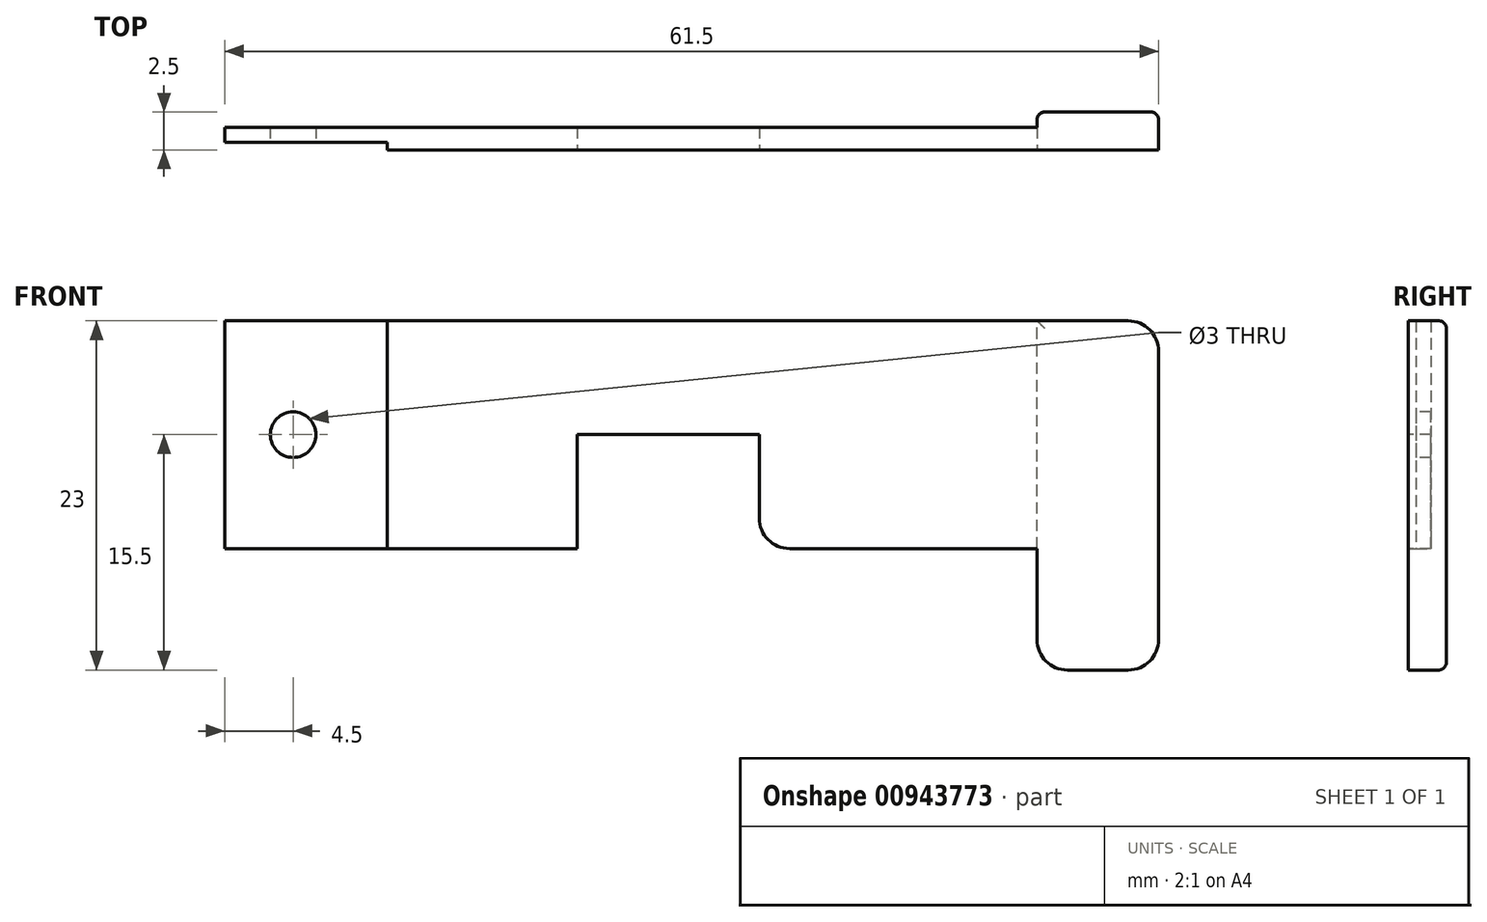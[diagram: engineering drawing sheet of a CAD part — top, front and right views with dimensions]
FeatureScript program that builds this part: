
annotation { "Feature Type Name" : "Feature", "Feature Type Description" : "" }
export const myFeature = defineFeature(function(context is Context, id is Id, definition is map)
    precondition{}
    {
        {
            var Q0;
            Q0=qCreatedBy(makeId("Front.planeOp"),FACE);
            var sketch = newSketch(context, id + "F0", { "sketchPlane" : qUnion([Q0])});
            skLineSegment(sketch, "E0.bottom", {"start": v(-38.5, 7.5) * mm, "end": v(25, 7.5) * mm});
            skLineSegment(sketch, "E0.top", {"start": v(-38.5, -7.5) * mm, "end": v(25, -7.5) * mm});
            skLineSegment(sketch, "E0.left", {"start": v(-38.5, 7.5) * mm, "end": v(-38.5, -7.5) * mm});
            skLineSegment(sketch, "E0.right", {"start": v(25, 7.5) * mm, "end": v(25, -7.5) * mm});
            skPoint(sketch, "E0.middle", {"position": v(-6.75, 0) * mm});
            skSolve(sketch);
        }
        {
            var Q0;
            Q0=qSketchRegion(id+"F0",true);
            extrude(context, id + "F1", {"entities" : qUnion([Q0]), "depth" : 1.5 * mm, "offsetDistance" : 25 * mm});
        }
        {
            var Q0;
            Q0=makeQuery(id+"F1.opExtrude","CAP_FACE",FACE,{"disambiguationData":[OSD([sQuery(id+"F0.wireOp",EDGE,"E0.bottom"),sQuery(id+"F0.wireOp",EDGE,"E0.top"),sQuery(id+"F0.wireOp",EDGE,"E0.left"),sQuery(id+"F0.wireOp",EDGE,"E0.right")])],"isStart":false});
            var sketch = newSketch(context, id + "F2", { "sketchPlane" : qUnion([Q0])});
            skLineSegment(sketch, "E1.bottom", {"start": v(25, -7.5) * mm, "end": v(15, -7.5) * mm});
            skLineSegment(sketch, "E1.top", {"start": v(25, -15.5) * mm, "end": v(15, -15.5) * mm});
            skLineSegment(sketch, "E1.left", {"start": v(25, -7.5) * mm, "end": v(25, -15.5) * mm});
            skLineSegment(sketch, "E1.right", {"start": v(15, -7.5) * mm, "end": v(15, -15.5) * mm});
            skSolve(sketch);
        }
        {
            var Q0;
            Q0=qSketchRegion(id+"F2",true);
            var Q1;
            Q1=makeQuery(id+"F1.opExtrude","CAP_FACE",FACE,{"disambiguationData":[OSD([sQuery(id+"F0.wireOp",EDGE,"E0.bottom"),sQuery(id+"F0.wireOp",EDGE,"E0.top"),sQuery(id+"F0.wireOp",EDGE,"E0.left"),sQuery(id+"F0.wireOp",EDGE,"E0.right")])],"isStart":true});
            extrude(context, id + "F3", {"entities" : qUnion([Q0]), "operationType" : NewBodyOperationType.ADD, "endBound" : BoundingType.UP_TO_SURFACE, "oppositeDirection" : true, "depth" : 25 * mm, "endBoundEntityFace" : qUnion([Q1]), "offsetDistance" : 25 * mm});
        }
        {
            var Q0;
            Q0=makeQuery(id+"F3.boolean.opBoolean","MERGE",FACE,{"derivedFrom":[makeQuery(id+"F1.opExtrude","CAP_FACE",FACE,{"disambiguationData":[OSD([sQuery(id+"F0.wireOp",EDGE,"E0.bottom"),sQuery(id+"F0.wireOp",EDGE,"E0.top"),sQuery(id+"F0.wireOp",EDGE,"E0.left"),sQuery(id+"F0.wireOp",EDGE,"E0.right")])],"isStart":false}),makeQuery(id+"F3.opExtrude","CAP_FACE",FACE,{"disambiguationData":[OSD([sQuery(id+"F2.wireOp",EDGE,"E1.bottom"),sQuery(id+"F2.wireOp",EDGE,"E1.top"),sQuery(id+"F2.wireOp",EDGE,"E1.left"),sQuery(id+"F2.wireOp",EDGE,"E1.right")])],"isStart":true})]});
            var sketch = newSketch(context, id + "F4", { "sketchPlane" : qUnion([Q0])});
            skLineSegment(sketch, "E2.bottom", {"start": v(-15.3, -7.5) * mm, "end": v(-3.3, -7.5) * mm});
            skLineSegment(sketch, "E2.top", {"start": v(-15.3, 0) * mm, "end": v(-3.3, 0) * mm});
            skLineSegment(sketch, "E2.left", {"start": v(-15.3, -7.5) * mm, "end": v(-15.3, 0) * mm});
            skLineSegment(sketch, "E2.right", {"start": v(-3.3, -7.5) * mm, "end": v(-3.3, 0) * mm});
            skSolve(sketch);
        }
        {
            var Q0;
            Q0=qSketchRegion(id+"F4",true);
            extrude(context, id + "F5", {"entities" : qUnion([Q0]), "operationType" : NewBodyOperationType.REMOVE, "endBound" : BoundingType.THROUGH_ALL, "oppositeDirection" : true, "depth" : 25 * mm, "offsetDistance" : 25 * mm});
        }
        {
            var Q0;
            Q0=makeQuery(id+"F3.boolean.opBoolean","MERGE",FACE,{"derivedFrom":[makeQuery(id+"F1.opExtrude","CAP_FACE",FACE,{"disambiguationData":[OSD([sQuery(id+"F0.wireOp",EDGE,"E0.bottom"),sQuery(id+"F0.wireOp",EDGE,"E0.top"),sQuery(id+"F0.wireOp",EDGE,"E0.left"),sQuery(id+"F0.wireOp",EDGE,"E0.right")])],"isStart":false}),makeQuery(id+"F3.opExtrude","CAP_FACE",FACE,{"disambiguationData":[OSD([sQuery(id+"F2.wireOp",EDGE,"E1.bottom"),sQuery(id+"F2.wireOp",EDGE,"E1.top"),sQuery(id+"F2.wireOp",EDGE,"E1.left"),sQuery(id+"F2.wireOp",EDGE,"E1.right")])],"isStart":true})]});
            var sketch = newSketch(context, id + "F6", { "sketchPlane" : qUnion([Q0])});
            skCircle(sketch, "E3", {"center": v(-34, 0) * mm, "radius": 1.5 * mm});
            skSolve(sketch);
        }
        {
            var Q0;
            Q0=qSketchRegion(id+"F6",true);
            extrude(context, id + "F7", {"entities" : qUnion([Q0]), "operationType" : NewBodyOperationType.REMOVE, "endBound" : BoundingType.THROUGH_ALL, "oppositeDirection" : true, "depth" : 25 * mm, "offsetDistance" : 25 * mm});
        }
        {
            var Q0;
            {var subQ1=sQuery(id+"F0.wireOp",EDGE,"E0.left");var subQ2=sQuery(id+"F0.wireOp",EDGE,"E0.top");Q0=makeQuery(id+"F5.boolean.opBoolean","SPLIT",FACE,{"disambiguationData":[TD([makeQuery(id+"F1.opExtrude","SWEPT_FACE",FACE,{"disambiguationData":[OSD([subQ1])]})])],"derivedFrom":makeQuery(id+"F1.opExtrude","SWEPT_FACE",FACE,{"disambiguationData":[OSD([subQ2])]})});}
            var sketch = newSketch(context, id + "F8", { "sketchPlane" : qUnion([Q0])});
            skPoint(sketch, "E4.oppositeSnap0", {"position": v(-38.5, 1) * mm});
            skLineSegment(sketch, "E4.bottom", {"start": v(-38.5, 1.5) * mm, "end": v(-27.8, 1.5) * mm});
            skLineSegment(sketch, "E4.top", {"start": v(-38.5, 1) * mm, "end": v(-27.8, 1) * mm});
            skLineSegment(sketch, "E4.left", {"start": v(-38.5, 1.5) * mm, "end": v(-38.5, 1) * mm});
            skLineSegment(sketch, "E4.right", {"start": v(-27.8, 1.5) * mm, "end": v(-27.8, 1) * mm});
            skSolve(sketch);
        }
        {
            var Q0;
            Q0=qSketchRegion(id+"F8",true);
            extrude(context, id + "F9", {"entities" : qUnion([Q0]), "operationType" : NewBodyOperationType.REMOVE, "endBound" : BoundingType.THROUGH_ALL, "oppositeDirection" : true, "depth" : 25 * mm, "offsetDistance" : 25 * mm});
        }
        {
            var Q0;
            Q0=makeQuery(id+"F3.opExtrude","SWEPT_FACE",FACE,{"disambiguationData":[OSD([sQuery(id+"F2.wireOp",EDGE,"E1.top")])]});
            var sketch = newSketch(context, id + "F10", { "sketchPlane" : qUnion([Q0])});
            skLineSegment(sketch, "E5.bottom", {"start": v(25, 1.5) * mm, "end": v(23, 1.5) * mm});
            skLineSegment(sketch, "E5.top", {"start": v(25, 0) * mm, "end": v(23, 0) * mm});
            skLineSegment(sketch, "E5.left", {"start": v(25, 1.5) * mm, "end": v(25, 0) * mm});
            skLineSegment(sketch, "E5.right", {"start": v(23, 1.5) * mm, "end": v(23, 0) * mm});
            skSolve(sketch);
        }
        {
            var Q0;
            Q0=qSketchRegion(id+"F10",true);
            extrude(context, id + "F11", {"entities" : qUnion([Q0]), "operationType" : NewBodyOperationType.REMOVE, "endBound" : BoundingType.THROUGH_ALL, "oppositeDirection" : true, "depth" : 25 * mm, "offsetDistance" : 25 * mm});
        }
        {
            var Q0;
            {var subQ0=sQuery(id+"F0.wireOp",EDGE,"E0.right");var subQ1=sQuery(id+"F0.wireOp",EDGE,"E0.left");var subQ2=sQuery(id+"F0.wireOp",EDGE,"E0.top");var subQ3=sQuery(id+"F0.wireOp",EDGE,"E0.bottom");Q0=makeQuery(id+"F3.boolean.opBoolean","MERGE",FACE,{"derivedFrom":[makeQuery(id+"F1.opExtrude","CAP_FACE",FACE,{"disambiguationData":[OSD([subQ3,subQ2,subQ1,subQ0])],"isStart":true}),makeQuery(id+"F3.opExtrude","CAP_FACE",FACE,{"disambiguationData":[OSD([subQ3,subQ2,subQ1,subQ0])],"isStart":false})]});}
            var sketch = newSketch(context, id + "F12", { "sketchPlane" : qUnion([Q0])});
            skPoint(sketch, "E6.oppositeSnap0", {"position": v(-15, -11.5) * mm});
            skLineSegment(sketch, "E6.bottom", {"start": v(-23, -15.5) * mm, "end": v(-15, -15.5) * mm});
            skLineSegment(sketch, "E6.top", {"start": v(-23, 7.5) * mm, "end": v(-15, 7.5) * mm});
            skLineSegment(sketch, "E6.left", {"start": v(-23, -15.5) * mm, "end": v(-23, 7.5) * mm});
            skLineSegment(sketch, "E6.right", {"start": v(-15, -15.5) * mm, "end": v(-15, 7.5) * mm});
            skSolve(sketch);
        }
        {
            var Q0;
            Q0=qSketchRegion(id+"F12",true);
            extrude(context, id + "F13", {"entities" : qUnion([Q0]), "operationType" : NewBodyOperationType.ADD, "depth" : 1 * mm, "offsetDistance" : 25 * mm});
        }
        {
            var Q0;
            Q0=makeQuery(id+"F13.boolean.opBoolean","MERGE",EDGE,{"derivedFrom":[makeQuery(id+"F3.opExtrude","SWEPT_EDGE",EDGE,{"disambiguationData":[OSD([sQuery(id+"F2.wireOp",EDGE,"E1.top"),sQuery(id+"F2.wireOp",EDGE,"E1.right")])]}),makeQuery(id+"F13.opExtrude","SWEPT_EDGE",EDGE,{"disambiguationData":[OSD([sQuery(id+"F12.wireOp",EDGE,"E6.bottom"),sQuery(id+"F12.wireOp",EDGE,"E6.right")])]})]});
            var Q1;
            Q1=makeQuery(id+"F13.boolean.opBoolean","MERGE",EDGE,{"derivedFrom":[makeQuery(id+"F11.boolean.opBoolean","COPY",EDGE,{"derivedFrom":makeQuery(id+"F11.opExtrude","CAP_EDGE",EDGE,{"disambiguationData":[OSD([sQuery(id+"F10.wireOp",EDGE,"E5.right")])],"isStart":true})}),makeQuery(id+"F13.opExtrude","SWEPT_EDGE",EDGE,{"disambiguationData":[OSD([sQuery(id+"F12.wireOp",EDGE,"E6.bottom"),sQuery(id+"F12.wireOp",EDGE,"E6.left")])]})]});
            var Q2;
            Q2=makeQuery(id+"F13.boolean.opBoolean","MERGE",EDGE,{"derivedFrom":[makeQuery(id+"F11.boolean.opBoolean","INTERSECT",EDGE,{"derivedFrom":[makeQuery(id+"F1.opExtrude","SWEPT_FACE",FACE,{"disambiguationData":[OSD([sQuery(id+"F0.wireOp",EDGE,"E0.bottom")])]}),makeQuery(id+"F11.opExtrude","SWEPT_FACE",FACE,{"disambiguationData":[OSD([sQuery(id+"F10.wireOp",EDGE,"E5.right")])]})]}),makeQuery(id+"F13.opExtrude","SWEPT_EDGE",EDGE,{"disambiguationData":[OSD([sQuery(id+"F12.wireOp",EDGE,"E6.top"),sQuery(id+"F12.wireOp",EDGE,"E6.left")])]})]});
            var Q3;
            Q3=makeQuery(id+"F5.boolean.opBoolean","COPY",EDGE,{"derivedFrom":makeQuery(id+"F5.opExtrude","SWEPT_EDGE",EDGE,{"disambiguationData":[OSD([sQuery(id+"F0.wireOp",EDGE,"E0.top"),sQuery(id+"F4.wireOp",EDGE,"E2.bottom"),sQuery(id+"F4.wireOp",EDGE,"E2.right")])]})});
            var Q4;
            Q4=makeQuery(id+"F5.boolean.opBoolean","COPY",EDGE,{"derivedFrom":makeQuery(id+"F5.opExtrude","SWEPT_EDGE",EDGE,{"disambiguationData":[OSD([sQuery(id+"F0.wireOp",EDGE,"E0.top"),sQuery(id+"F4.wireOp",EDGE,"E2.bottom"),sQuery(id+"F4.wireOp",EDGE,"E2.left")])]})});
            fillet(context, id + "F14", {"entities" : qUnion([Q0, Q1, Q2, Q3, Q4]), "radius" : 2 * mm, "tangentPropagation" : true, "allowEdgeOverflow" : false});
        }
        {
            var Q0;
            Q0=makeQuery(id+"F13.opExtrude","CAP_EDGE",EDGE,{"disambiguationData":[OSD([sQuery(id+"F12.wireOp",EDGE,"E6.left")])],"isStart":false});
            var Q1;
            Q1=makeQuery(id+"F11.boolean.opBoolean","COPY",EDGE,{"derivedFrom":makeQuery(id+"F11.opExtrude","SWEPT_EDGE",EDGE,{"disambiguationData":[OSD([sQuery(id+"F2.wireOp",EDGE,"E1.top"),sQuery(id+"F10.wireOp",EDGE,"E5.bottom"),sQuery(id+"F10.wireOp",EDGE,"E5.right")])]})});
            fillet(context, id + "F15", {"entities" : qUnion([Q0, Q1]), "radius" : 0.5 * mm, "tangentPropagation" : true, "allowEdgeOverflow" : false});
        }
    });
